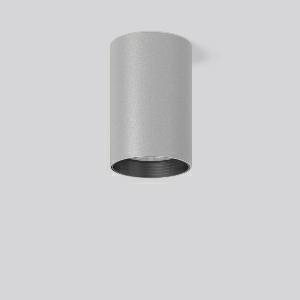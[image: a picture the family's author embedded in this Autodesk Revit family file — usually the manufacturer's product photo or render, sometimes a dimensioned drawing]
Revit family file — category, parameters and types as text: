
# Revit family: heledon_maxi_a_931229_004_3_76_b82d
name_source: partatom
category: Lighting Fixtures
units: mm (PartAtom-declared; Revit-internal decimal feet)

## family parameters
Cut with Voids When Loaded = No
Host = Face
Light Source = No
Part Type = Normal
Room Calculation Point = No
Round Connector Dimension = Use Diameter
Shared = No

## types (1)
- HELEDON maxi A (1 x LED Modul 935, 3650 lm, 3500)
    Apparent Load = 35 VA
    Approval mark = CE
    CIE Flux Codes = 96 100 100 100 100
    Color Rendering = 92
    Color Temperature = 3500
    Default Elevation = 1800 mm
    Description = Series: HELEDON maxi
Cylindrical surface-mounted downlight. Housing: die-cast aluminium, powder-coated. Internal ceiling frame polycarbonate with bayonet mounting. Black plastic ring and recessed LED to prevent glare from the side. Optical assembly with lens made of plastic (polycarbonate) for the best homogeneous light distribution - can be changed without tools. Best colour rendering index Ra>90. Suitable for Ceiling mounting. Easy installation with a separate ceiling frame with bayonet mounting and plug connection. Driver integrated. Connected via plug-in connector. High quality converter without flickering and stroboscopic effect. The following accessories can be mounted without use of tools: interchangeable lenses, decorative glasses, honeycomb louvre, clear and frosted diffusers, white interchangeable plastic ring. 
Colour: silver
Diameter: 123 mm
Height: 183 mm
Lamp: LED
Socket: without socket
Colour temperature: 3500K
Colour rendering index (CRI): 92
System power: 35 W
Rated luminous flux: 3650 lm
Luminous efficiency: 104 lm/W
Control gear: Converter, dimmable, DALI
Protection class: I
Type of protection: IP 20
    Height = 183 mm
    Lamp = 1 x LED Modul 935
    Lamp Light Flux = 3650 lm
    Lamp count = 1
    Length = 123 mm
    Lifetime = 50000 h
    Luminous efficacy = 104 lm/W
    Manufacturer = RZB
    ModVariant = No
    Model = 931229.004.3.76
    Mounting Place = Ceiling
    Mounting Type = Surface mounted
    Number of Poles = 1
    OnlyDefault = Yes
    Power Factor = 1
    Product Name = HELEDON maxi A
    Product group = Surface mounted downlights
    ProductGroupID = 302
    Protection Class = Protection class I
    Protection Degree = IP 20
    RLX_Detail_Level = 1
    RLX_Emergency_Light_Flux = 0 lm
    RLX_Emergency_Type = 0
    RLX_Emergency_Type_DB = No
    RlxData = <blob elided: 98413 chars, md5=85062a44>
    Socket = socket
    Standby Power = 0 W
    System Light Flux = 3650 lm
    System Power = 35 W
    Type Comments = Product without accessories
    Type Image = 931193.004.jpg
    URL = http://relux.com
    VarID = ---
    Voltage = 230 V
    Voltage Range = 220-240 V
    Weight = 0.00 kg
    Width = 0 mm  [stored 0 ft]

note: [stored X ft] marks values corroborated as IEEE doubles in the binary element streams (Revit-internal decimal feet)

## geometry (parser evidence)
native form markers: Blend x4, Sweep x9
no freeform markers — native parametric forms only
